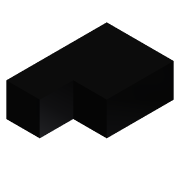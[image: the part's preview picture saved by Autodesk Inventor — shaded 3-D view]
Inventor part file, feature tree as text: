
AUTODESK INVENTOR PART (.ipt)
format: ipt  version: 2015 (Build 190159000, 159)  size: 77,312 bytes
history: native  units: in
note: dims shown in document units (in); Inventor stores cm internally (conversion verified against a paired STEP export)
features: extrude x1, sketch x1
ambient origin geometry x8: Origin, YZ Plane, XZ Plane, XY Plane, X Axis, Y Axis, Z Axis, Center Point
bodies: Solid1 (feature_tree)
feature tree (2):
  extrude  "Extrusion1"  Depth=2.0in
  sketch  "Sketch1"  dims[d0=3.0in d1=2.0in d2=2.0in d3=1.0in d4=1.0in d5=0.0in]
